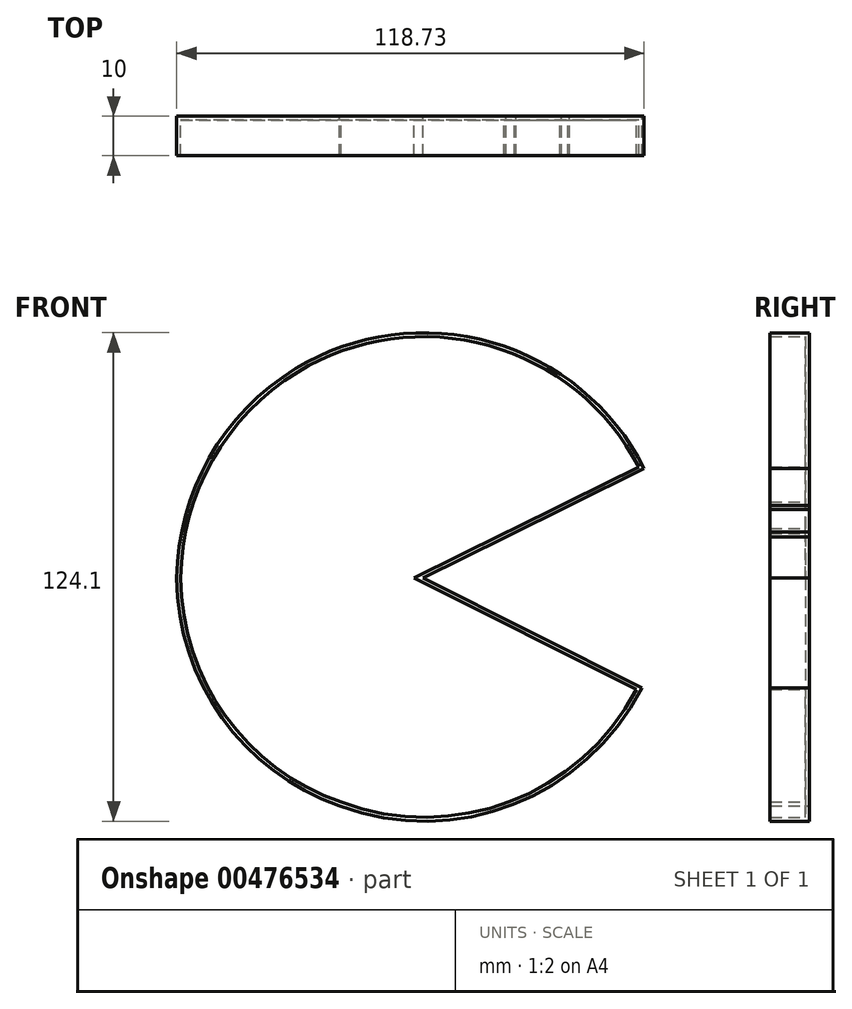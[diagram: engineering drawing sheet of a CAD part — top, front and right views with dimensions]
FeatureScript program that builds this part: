
annotation { "Feature Type Name" : "Feature", "Feature Type Description" : "" }
export const myFeature = defineFeature(function(context is Context, id is Id, definition is map)
    precondition{}
    {
        {
            var Q0;
            Q0=qCreatedBy(makeId("Front.planeOp"),FACE);
            var sketch = newSketch(context, id + "F0", { "sketchPlane" : qUnion([Q0])});
            skLineSegment(sketch, "E0", {"start": v(0, 0) * mm, "end": v(21.03, 10.48) * mm});
            skLineSegment(sketch, "E1", {"start": v(21.03, 10.48) * mm, "end": v(23.64, 11.74) * mm});
            skLineSegment(sketch, "E2", {"start": v(23.64, 11.74) * mm, "end": v(35.24, 17.5) * mm});
            skLineSegment(sketch, "E3", {"start": v(35.24, 17.5) * mm, "end": v(37.2, 18.44) * mm});
            skLineSegment(sketch, "E4", {"start": v(37.2, 18.44) * mm, "end": v(40.1, 19.87) * mm});
            skLineSegment(sketch, "E5", {"start": v(40.1, 19.87) * mm, "end": v(56.18, 27.85) * mm});
            skLineSegment(sketch, "E6", {"start": v(0, 0) * mm, "end": v(55.58, -27.89) * mm});
            skArc(sketch, "E7", {"start": v(56.18, 27.85) * mm, "mid": v(17.49, 59.91) * mm, "end": v(-32.32, 53.26) * mm});
            skArc(sketch, "E8", {"start": v(-32.32, 53.26) * mm, "mid": v(-54.32, 30.54) * mm, "end": v(-62.55, 0) * mm});
            skArc(sketch, "E9", {"start": v(-62.55, 0) * mm, "mid": v(-51.06, -35.5) * mm, "end": v(-21.19, -57.84) * mm});
            skArc(sketch, "E10", {"start": v(-21.19, -57.84) * mm, "mid": v(22.91, -57.52) * mm, "end": v(55.58, -27.89) * mm});
            skSolve(sketch);
        }
        {
            var Q0;
            Q0=makeQuery(id+"F0.imprint","IMPRINT",FACE,{"disambiguationData":[TD([[makeQuery(id+"F0.imprint","IMPRINT",EDGE,{"derivedFrom":sQuery(id+"F0.wireOp",EDGE,"E0")}),1.0]])]});
            extrude(context, id + "F1", {"entities" : qUnion([Q0]), "depth" : 10 * mm});
        }
        {
            var Q0;
            Q0=makeQuery(id+"F1.opExtrude","CAP_FACE",FACE,{"disambiguationData":[OSD([sQuery(id+"F0.wireOp",EDGE,"E0"),sQuery(id+"F0.wireOp",EDGE,"E1"),sQuery(id+"F0.wireOp",EDGE,"E2"),sQuery(id+"F0.wireOp",EDGE,"E3"),sQuery(id+"F0.wireOp",EDGE,"E4"),sQuery(id+"F0.wireOp",EDGE,"E5"),sQuery(id+"F0.wireOp",EDGE,"E6"),sQuery(id+"F0.wireOp",EDGE,"E7"),sQuery(id+"F0.wireOp",EDGE,"E8"),sQuery(id+"F0.wireOp",EDGE,"E9"),sQuery(id+"F0.wireOp",EDGE,"E10")])],"isStart":false});
            shell(context, id + "F2", {"entities" : qUnion([Q0]), "thickness" : 1 * mm});
        }
    });
